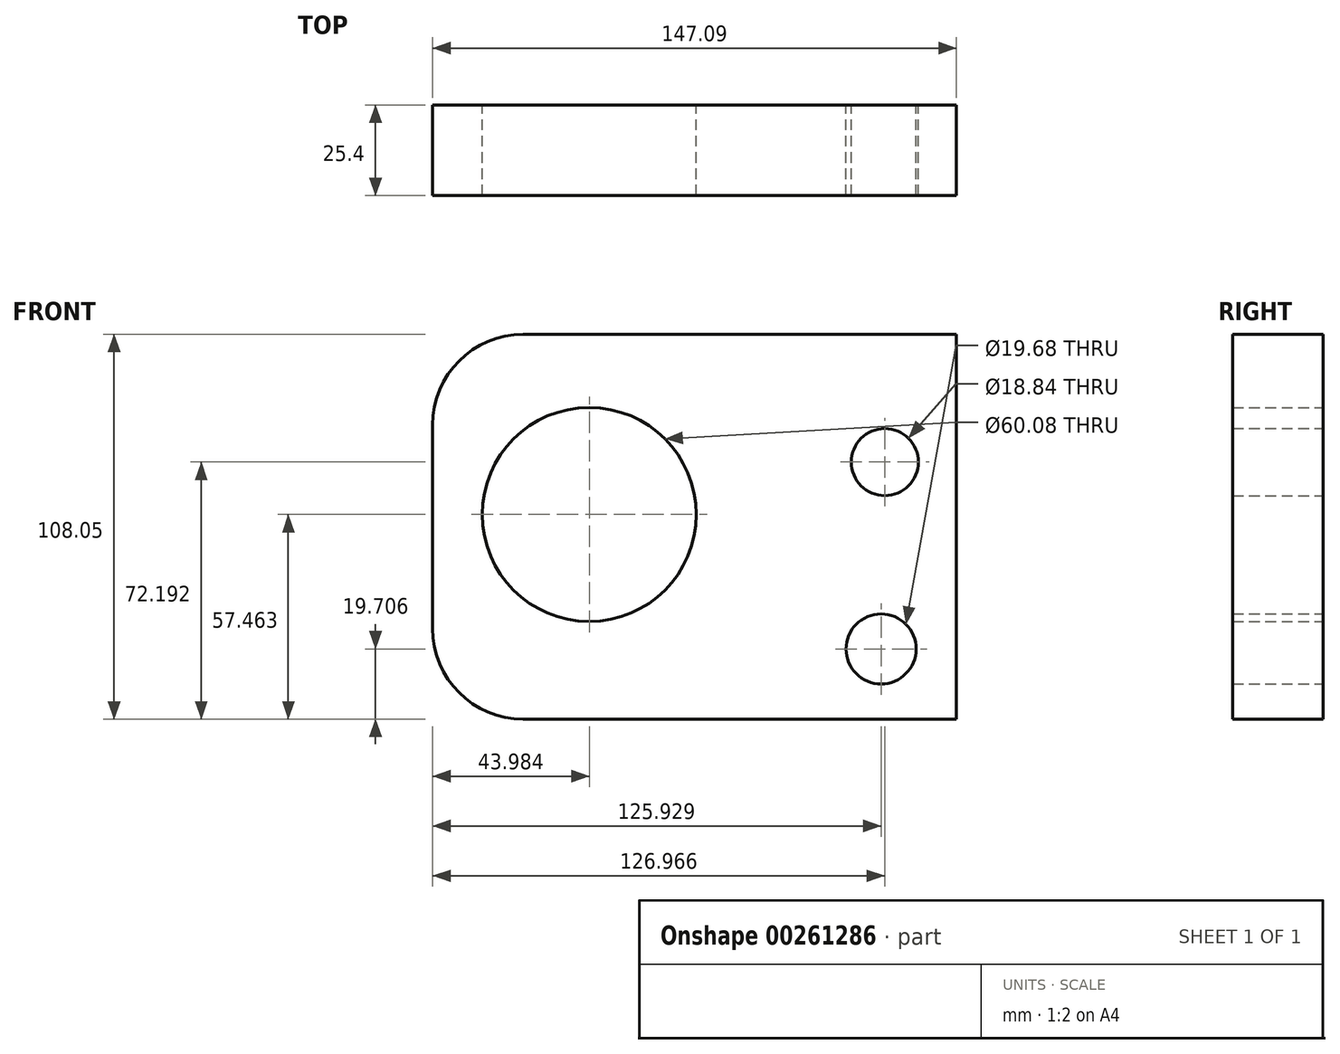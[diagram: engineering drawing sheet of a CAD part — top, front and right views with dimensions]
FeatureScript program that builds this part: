
annotation { "Feature Type Name" : "Feature", "Feature Type Description" : "" }
export const myFeature = defineFeature(function(context is Context, id is Id, definition is map)
    precondition{}
    {
        {
            var Q0;
            Q0=qCreatedBy(makeId("Front.planeOp"),FACE);
            var sketch = newSketch(context, id + "F0", { "sketchPlane" : qUnion([Q0])});
            skLineSegment(sketch, "E0.bottom", {"start": v(-48.25, 60.96) * mm, "end": v(73.44, 60.96) * mm});
            skLineSegment(sketch, "E0.top", {"start": v(-48.25, -47.1) * mm, "end": v(73.44, -47.1) * mm});
            skLineSegment(sketch, "E0.left", {"start": v(-73.65, 35.56) * mm, "end": v(-73.65, -21.7) * mm});
            skLineSegment(sketch, "E0.right", {"start": v(73.44, 60.96) * mm, "end": v(73.44, -47.1) * mm});
            skCircle(sketch, "E1", {"center": v(53.32, 25.1) * mm, "radius": 9.42 * mm});
            skCircle(sketch, "E2", {"center": v(52.28, -27.38) * mm, "radius": 9.84 * mm});
            skPoint(sketch, "E3.visualSharp", {"position": v(-73.65, 60.96) * mm});
            skArc(sketch, "E3.filletArc", {"start": v(-48.25, 60.96) * mm, "mid": v(-66.2, 53.52) * mm, "end": v(-73.65, 35.56) * mm});
            skPoint(sketch, "E4.visualSharp", {"position": v(-73.65, -47.1) * mm});
            skArc(sketch, "E4.filletArc", {"start": v(-73.65, -21.7) * mm, "mid": v(-66.2, -39.65) * mm, "end": v(-48.25, -47.1) * mm});
            skCircle(sketch, "E5", {"center": v(-29.67, 10.37) * mm, "radius": 30.04 * mm});
            skSolve(sketch);
        }
        {
            var Q0;
            Q0=makeQuery(id+"F0.imprint","IMPRINT",FACE,{"disambiguationData":[TD([[makeQuery(id+"F0.imprint","IMPRINT",EDGE,{"derivedFrom":sQuery(id+"F0.wireOp",EDGE,"E0.bottom")}),-1.0]])]});
            extrude(context, id + "F1", {"entities" : qUnion([Q0]), "depth" : 25.4 * mm});
        }
    });
